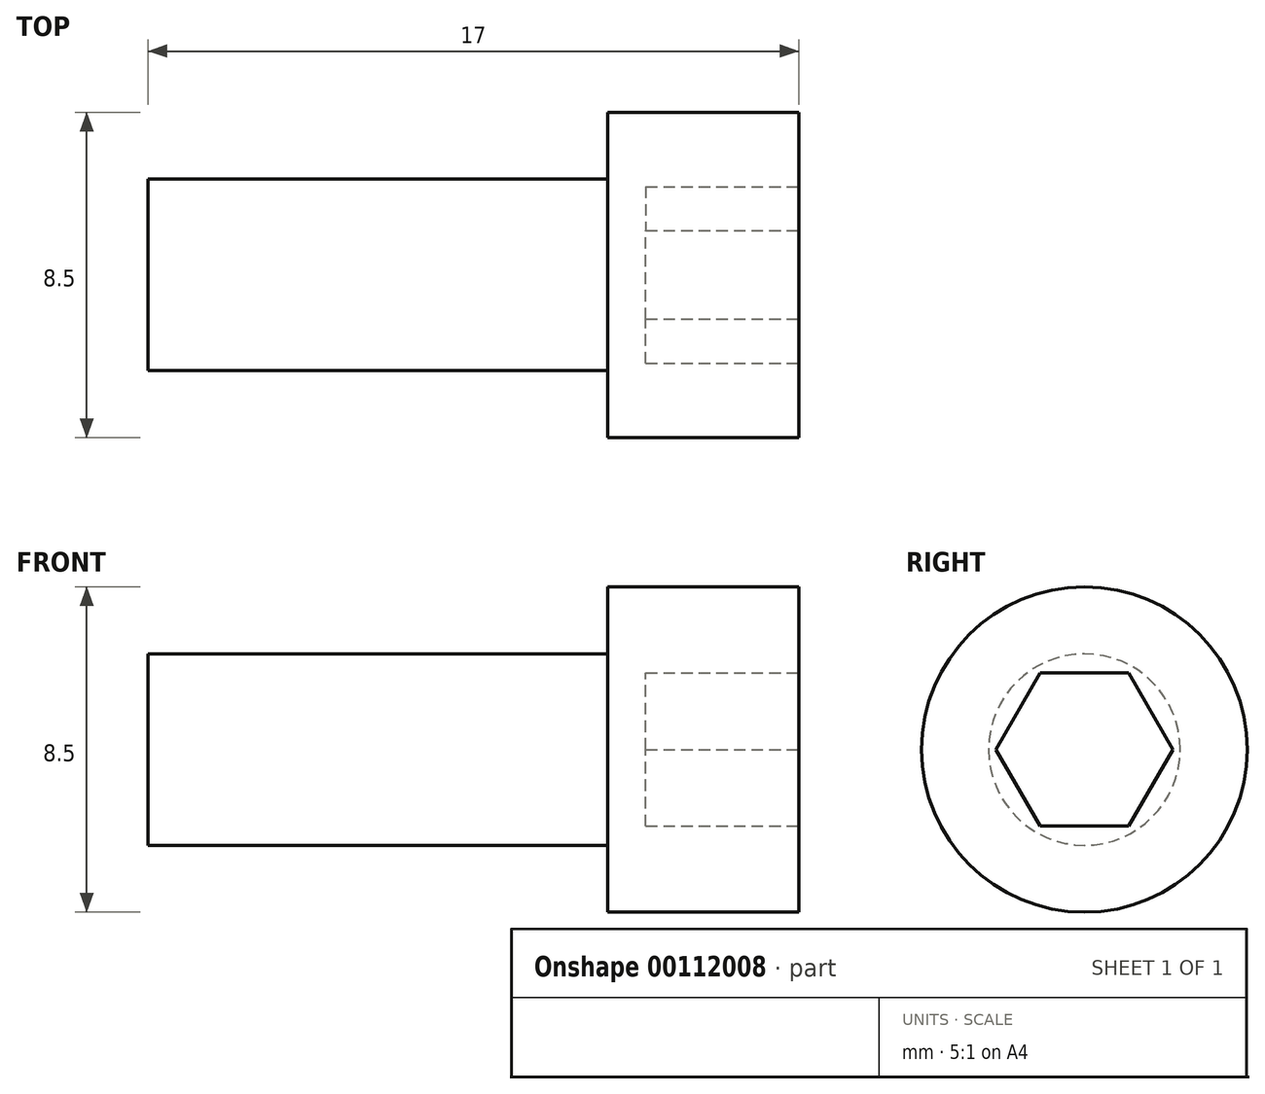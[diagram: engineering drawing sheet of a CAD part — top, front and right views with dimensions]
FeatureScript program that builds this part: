
annotation { "Feature Type Name" : "Feature", "Feature Type Description" : "" }
export const myFeature = defineFeature(function(context is Context, id is Id, definition is map)
    precondition{}
    {
        {
            var Q0;
            Q0=qCreatedBy(makeId("Front.planeOp"),FACE);
            var sketch = newSketch(context, id + "F0", { "sketchPlane" : qUnion([Q0])});
            skLineSegment(sketch, "E0", {"start": v(0, 0) * mm, "end": v(0, 2.5) * mm});
            skLineSegment(sketch, "E1", {"start": v(0, 2.5) * mm, "end": v(12, 2.5) * mm});
            skLineSegment(sketch, "E2", {"start": v(12, 2.5) * mm, "end": v(12, 4.25) * mm});
            skLineSegment(sketch, "E3", {"start": v(12, 4.25) * mm, "end": v(17, 4.25) * mm});
            skLineSegment(sketch, "E4", {"start": v(17, 4.25) * mm, "end": v(17, 0) * mm});
            skLineSegment(sketch, "E5", {"start": v(17, 0) * mm, "end": v(0, 0) * mm});
            skSolve(sketch);
        }
        {
            var Q0;
            Q0=makeQuery(id+"F0.imprint","IMPRINT",FACE,{"disambiguationData":[TD([[makeQuery(id+"F0.imprint","IMPRINT",EDGE,{"derivedFrom":sQuery(id+"F0.wireOp",EDGE,"E0")}),-1.0]])]});
            var Q1;
            Q1=sQuery(id+"F0.wireOp",EDGE,"E5");
            revolve(context, id + "F1", {"entities" : qUnion([Q0]), "axis" : qUnion([Q1]), "revolveType" : RevolveType.FULL});
        }
        {
            var Q0;
            Q0=makeQuery(id+"F1.opRevolve","SWEPT_FACE",FACE,{"disambiguationData":[OSD([sQuery(id+"F0.wireOp",EDGE,"E4")])]});
            var sketch = newSketch(context, id + "F2", { "sketchPlane" : qUnion([Q0])});
            skCircle(sketch, "E6.cCircle", {"center": v(0, 0) * mm, "radius": 2 * mm, "construction": true});
            skLineSegment(sketch, "E6.0", {"start": v(-1.15, 2) * mm, "end": v(1.15, 2) * mm});
            skLineSegment(sketch, "E6.1", {"start": v(1.15, 2) * mm, "end": v(2.3, 0) * mm});
            skLineSegment(sketch, "E6.2", {"start": v(2.3, 0) * mm, "end": v(1.15, -2) * mm});
            skLineSegment(sketch, "E6.3", {"start": v(1.15, -2) * mm, "end": v(-1.15, -2) * mm});
            skLineSegment(sketch, "E6.4", {"start": v(-1.15, -2) * mm, "end": v(-2.3, 0) * mm});
            skLineSegment(sketch, "E6.5", {"start": v(-2.3, 0) * mm, "end": v(-1.15, 2) * mm});
            skPoint(sketch, "E6.0.midPoint", {"position": v(0, 2) * mm});
            skSolve(sketch);
        }
        {
            var Q0;
            Q0 = qSketchRegion(id + "F2", true);
            extrude(context, id + "F3", {"entities" : qUnion([Q0]), "operationType" : NewBodyOperationType.REMOVE, "oppositeDirection" : true, "depth" : 4 * mm});
        }
    });
